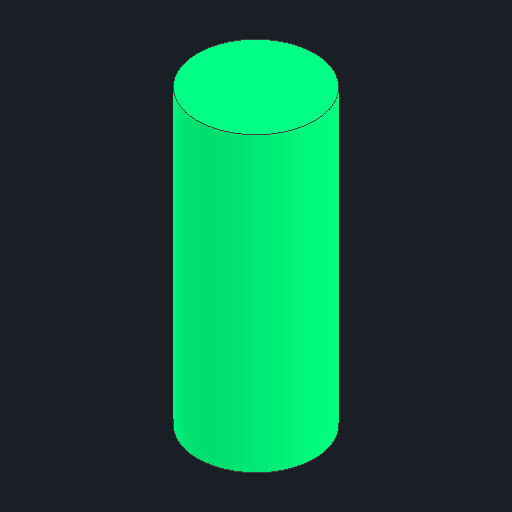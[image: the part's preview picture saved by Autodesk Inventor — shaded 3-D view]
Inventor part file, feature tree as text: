
AUTODESK INVENTOR PART (.ipt)
format: ipt  version: 2025.2 (Build 292293000, 293)  size: 84,480 bytes
history: native  units: in
note: dims shown in document units (in); Inventor stores cm internally (conversion verified against a paired STEP export)
features: other x3, sketch x1
ambient origin geometry x8: Origin, YZ Plane, XZ Plane, XY Plane, X Axis, Y Axis, Z Axis, Center Point
bodies: Solid1 (feature_tree)
feature tree (4):
  other  "26650(Green).ipt"
  other  "Solid1::26650(Green).ipt"
  other  "TaggingFeature1"
  sketch  "Sketch1"  dims[d0=0.3937in]
